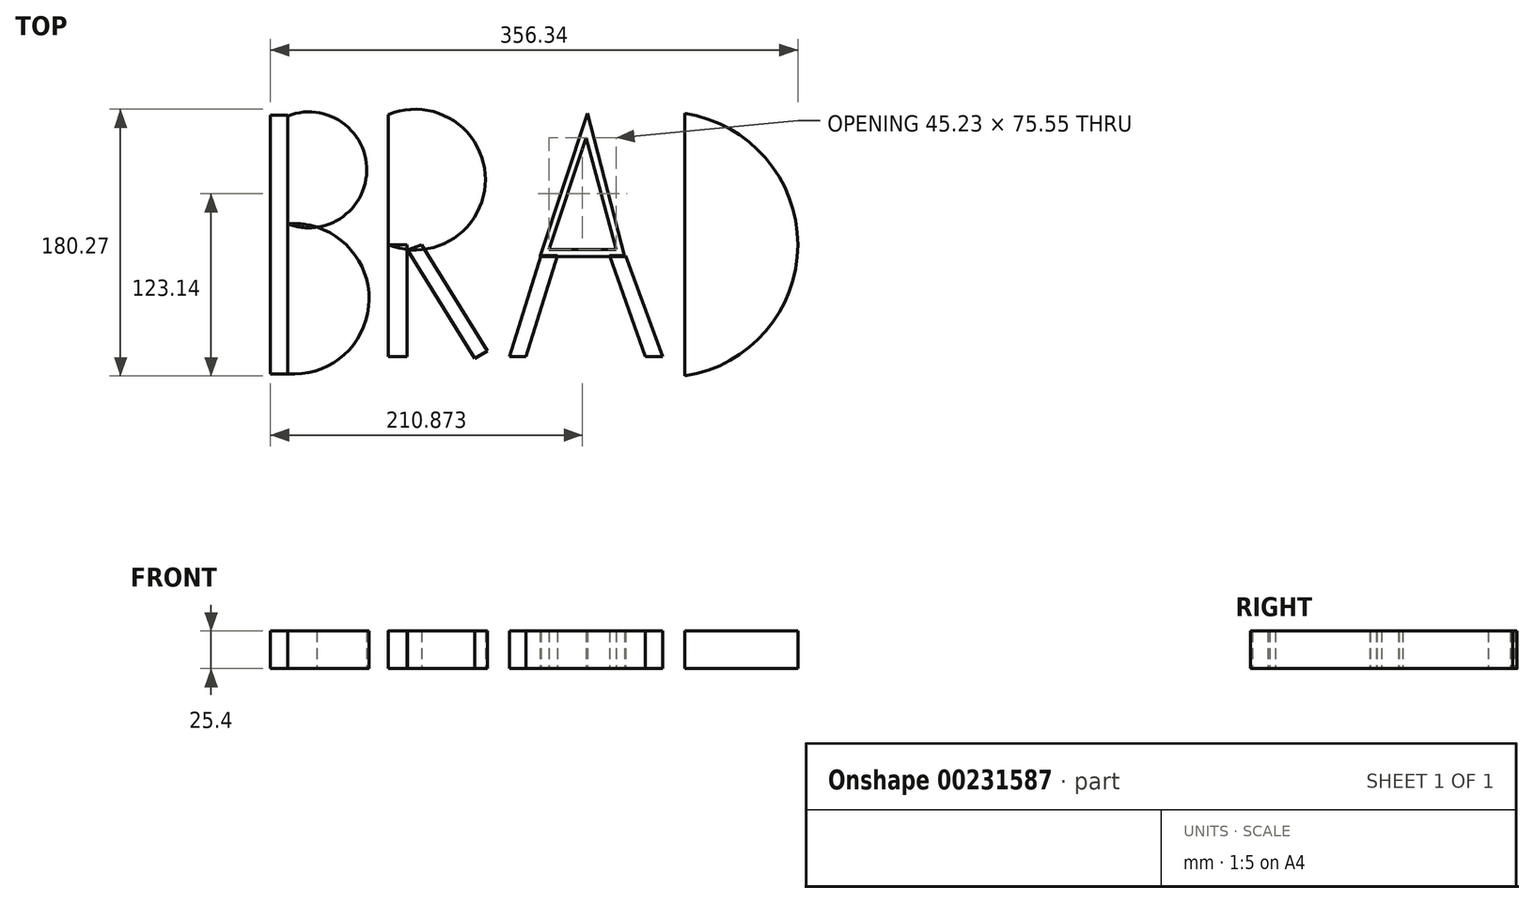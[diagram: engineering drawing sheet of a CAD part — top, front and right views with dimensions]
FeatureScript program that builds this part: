
annotation { "Feature Type Name" : "Feature", "Feature Type Description" : "" }
export const myFeature = defineFeature(function(context is Context, id is Id, definition is map)
    precondition{}
    {
        {
            var Q0;
            Q0=qCreatedBy(makeId("Top.planeOp"),FACE);
            var sketch = newSketch(context, id + "F0", { "sketchPlane" : qUnion([Q0])});
            skLineSegment(sketch, "E0", {"start": v(-144.17, 87.02) * mm, "end": v(-144.17, -87.4) * mm});
            skArc(sketch, "E1", {"start": v(-144.17, 14.08) * mm, "mid": v(-90.76, 50.55) * mm, "end": v(-144.17, 87.02) * mm});
            skArc(sketch, "E2", {"start": v(-144.17, -87.4) * mm, "mid": v(-89.2, -36.66) * mm, "end": v(-144.17, 14.08) * mm});
            skSolve(sketch);
        }
        {
            var Q0;
            Q0=qCreatedBy(makeId("Top.planeOp"),FACE);
            var sketch = newSketch(context, id + "F1", { "sketchPlane" : qUnion([Q0])});
            skLineSegment(sketch, "E3", {"start": v(-76.3, 87.92) * mm, "end": v(-76.3, -89.66) * mm});
            skArc(sketch, "E4", {"start": v(-76.3, 0) * mm, "mid": v(-10.61, 43.96) * mm, "end": v(-76.3, 87.92) * mm});
            skLineSegment(sketch, "E5", {"start": v(-76.3, 0) * mm, "end": v(-13.02, -88.26) * mm});
            skLineSegment(sketch, "E6", {"start": v(0, -88.26) * mm, "end": v(58.29, 88.62) * mm});
            skLineSegment(sketch, "E7", {"start": v(58.29, 88.62) * mm, "end": v(104.08, -87.21) * mm});
            skLineSegment(sketch, "E8", {"start": v(26.46, -7.97) * mm, "end": v(83.44, -7.97) * mm});
            skLineSegment(sketch, "E9", {"start": v(57.34, 72.15) * mm, "end": v(32.45, -3.4) * mm});
            skLineSegment(sketch, "E10", {"start": v(32.45, -3.4) * mm, "end": v(77.68, -3.4) * mm});
            skLineSegment(sketch, "E11", {"start": v(77.68, -3.4) * mm, "end": v(57.34, 72.15) * mm});
            skLineSegment(sketch, "E12", {"start": v(124.17, 88.62) * mm, "end": v(124.17, -88.76) * mm});
            skArc(sketch, "E13", {"start": v(124.17, -88.76) * mm, "mid": v(200.53, -0.07) * mm, "end": v(124.17, 88.62) * mm});
            skLineSegment(sketch, "E14", {"start": v(-144.43, 87.33) * mm, "end": v(-144.43, -86.13) * mm});
            skArc(sketch, "E15", {"start": v(-144.43, 13.21) * mm, "mid": v(-90.63, 50.27) * mm, "end": v(-144.43, 87.33) * mm});
            skArc(sketch, "E16", {"start": v(-144.43, -86.13) * mm, "mid": v(-89.05, -36.46) * mm, "end": v(-144.43, 13.21) * mm});
            skSolve(sketch);
        }
        {
            var Q0;
            {var subQ0=sQuery(id+"F0.wireOp",EDGE,"E1");var subQ1=sQuery(id+"F0.wireOp",EDGE,"E0");var subQ2=makeQuery(id+"F0.imprint","INTERSECT",VERTEX,{"derivedFrom":[subQ1,subQ0]});Q0=makeQuery(id+"F0.imprint","IMPRINT",FACE,{"disambiguationData":[TD([[makeQuery(id+"F0.imprint","IMPRINT",EDGE,{"disambiguationData":[TD([[subQ2,1.0]])],"derivedFrom":subQ0}),1.0]])]});}
            var Q1;
            {var subQ0=sQuery(id+"F0.wireOp",EDGE,"E2");var subQ1=sQuery(id+"F0.wireOp",EDGE,"E0");var subQ2=makeQuery(id+"F0.imprint","INTERSECT",VERTEX,{"derivedFrom":[subQ1,subQ0]});Q1=makeQuery(id+"F0.imprint","IMPRINT",FACE,{"disambiguationData":[TD([[makeQuery(id+"F0.imprint","IMPRINT",EDGE,{"disambiguationData":[TD([[subQ2,-1.0]])],"derivedFrom":subQ0}),1.0]])]});}
            var Q2;
            {var subQ0=sQuery(id+"F1.wireOp",EDGE,"E4");Q2=makeQuery(id+"F1.imprint","IMPRINT",FACE,{"disambiguationData":[TD([[makeQuery(id+"F1.imprint","IMPRINT",EDGE,{"derivedFrom":subQ0}),1.0]])]});}
            var Q3;
            {var subQ0=sQuery(id+"F1.wireOp",EDGE,"E8");Q3=makeQuery(id+"F1.imprint","IMPRINT",FACE,{"disambiguationData":[TD([[makeQuery(id+"F1.imprint","IMPRINT",EDGE,{"derivedFrom":subQ0}),1.0]])]});}
            var Q4;
            Q4=makeQuery(id+"F1.imprint","IMPRINT",FACE,{"disambiguationData":[TD([[makeQuery(id+"F1.imprint","IMPRINT",EDGE,{"derivedFrom":sQuery(id+"F1.wireOp",EDGE,"E12")}),1.0]])]});
            extrude(context, id + "F2", {"entities" : qUnion([Q0, Q1, Q2, Q3, Q4]), "depth" : 25.4 * mm});
        }
        {
            var Q0;
            Q0=qCreatedBy(makeId("Top.planeOp"),FACE);
            var sketch = newSketch(context, id + "F3", { "sketchPlane" : qUnion([Q0])});
            skLineSegment(sketch, "E17.bottom", {"start": v(-144.04, 87.37) * mm, "end": v(-155.81, 87.37) * mm});
            skLineSegment(sketch, "E17.top", {"start": v(-144.04, -87.43) * mm, "end": v(-155.81, -87.43) * mm});
            skLineSegment(sketch, "E17.left", {"start": v(-144.04, 87.37) * mm, "end": v(-144.04, -87.43) * mm});
            skLineSegment(sketch, "E17.right", {"start": v(-155.81, 87.37) * mm, "end": v(-155.81, -87.43) * mm});
            skLineSegment(sketch, "E18.bottom", {"start": v(-76.11, 0) * mm, "end": v(-63.43, 0) * mm});
            skLineSegment(sketch, "E18.top", {"start": v(-76.11, -75.66) * mm, "end": v(-63.43, -75.66) * mm});
            skLineSegment(sketch, "E18.left", {"start": v(-76.11, 0) * mm, "end": v(-76.11, -75.66) * mm});
            skLineSegment(sketch, "E18.right", {"start": v(-63.43, 0) * mm, "end": v(-63.43, -75.66) * mm});
            skSolve(sketch);
        }
        {
            var Q0;
            Q0=qCreatedBy(makeId("Top.planeOp"),FACE);
            var sketch = newSketch(context, id + "F4", { "sketchPlane" : qUnion([Q0])});
            skLineSegment(sketch, "E19", {"start": v(-63.19, -3.54) * mm, "end": v(-17.65, -77.07) * mm});
            skLineSegment(sketch, "E20", {"start": v(-17.65, -77.07) * mm, "end": v(-9.27, -71.88) * mm});
            skLineSegment(sketch, "E21", {"start": v(-9.27, -71.88) * mm, "end": v(-53.78, 0) * mm});
            skLineSegment(sketch, "E22", {"start": v(-53.78, 0) * mm, "end": v(-63.19, -3.54) * mm});
            skSolve(sketch);
        }
        {
            var Q0;
            Q0=qCreatedBy(makeId("Top.planeOp"),FACE);
            var sketch = newSketch(context, id + "F5", { "sketchPlane" : qUnion([Q0])});
            skLineSegment(sketch, "E23", {"start": v(26.87, -7.59) * mm, "end": v(5.62, -75.72) * mm});
            skLineSegment(sketch, "E24", {"start": v(5.62, -75.72) * mm, "end": v(16.75, -75.72) * mm});
            skLineSegment(sketch, "E25", {"start": v(16.75, -75.72) * mm, "end": v(38, -7.59) * mm});
            skLineSegment(sketch, "E26", {"start": v(38, -7.59) * mm, "end": v(26.87, -7.59) * mm});
            skLineSegment(sketch, "E27", {"start": v(84.22, -7.59) * mm, "end": v(109.18, -75.72) * mm});
            skPoint(sketch, "E27.startSnap0", {"position": v(32.44, -7.59) * mm});
            skLineSegment(sketch, "E28", {"start": v(109.18, -75.72) * mm, "end": v(97.37, -75.72) * mm});
            skLineSegment(sketch, "E29", {"start": v(97.37, -75.72) * mm, "end": v(73.42, -7.59) * mm});
            skLineSegment(sketch, "E30", {"start": v(73.42, -7.59) * mm, "end": v(84.22, -7.59) * mm});
            skSolve(sketch);
        }
        {
            var Q0;
            Q0 = qSketchRegion(id + "F5", true);
            var Q1;
            Q1 = qSketchRegion(id + "F4", true);
            var Q2;
            Q2 = qSketchRegion(id + "F3", true);
            extrude(context, id + "F6", {"entities" : qUnion([Q0, Q1, Q2]), "depth" : 25.4 * mm});
        }
    });
